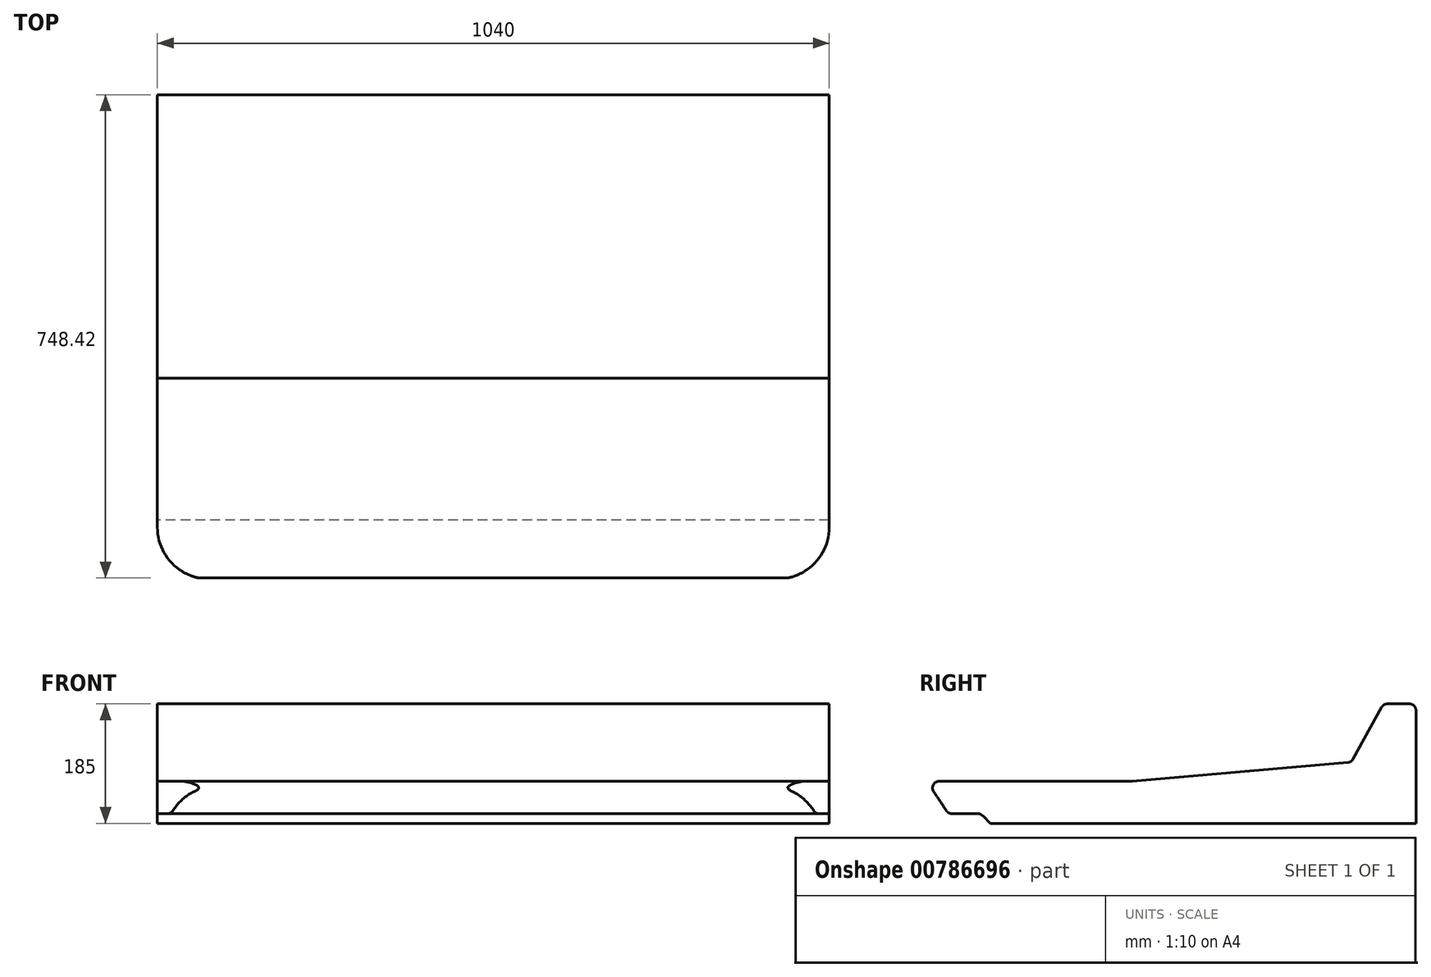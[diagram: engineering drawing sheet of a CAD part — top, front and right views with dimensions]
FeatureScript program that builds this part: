
annotation { "Feature Type Name" : "Feature", "Feature Type Description" : "" }
export const myFeature = defineFeature(function(context is Context, id is Id, definition is map)
    precondition{}
    {
        {
            var Q0;
            Q0=qCreatedBy(makeId("Right.planeOp"),FACE);
            var sketch = newSketch(context, id + "F0", { "sketchPlane" : qUnion([Q0])});
            skLineSegment(sketch, "E0", {"start": v(378, -92.5) * mm, "end": v(-281, -92.5) * mm});
            skLineSegment(sketch, "E1", {"start": v(-281, -92.5) * mm, "end": v(-293.07, -80.43) * mm});
            skLineSegment(sketch, "E2", {"start": v(-300.14, -77.5) * mm, "end": v(-340.62, -77.5) * mm});
            skLineSegment(sketch, "E3", {"start": v(-348.96, -73) * mm, "end": v(-368.76, -43) * mm});
            skLineSegment(sketch, "E4", {"start": v(-360.42, -27.5) * mm, "end": v(-61, -27.5) * mm});
            skLineSegment(sketch, "E5", {"start": v(-61, -27.5) * mm, "end": v(272.7, 1.7) * mm});
            skLineSegment(sketch, "E6", {"start": v(280.58, 6.81) * mm, "end": v(325.15, 87.34) * mm});
            skLineSegment(sketch, "E7", {"start": v(333.9, 92.5) * mm, "end": v(368, 92.5) * mm});
            skLineSegment(sketch, "E8", {"start": v(378, 82.5) * mm, "end": v(378, -92.5) * mm});
            skPoint(sketch, "E9.visualSharp", {"position": v(378, 92.5) * mm});
            skArc(sketch, "E9.filletArc", {"start": v(378, 82.5) * mm, "mid": v(375.07, 89.57) * mm, "end": v(368, 92.5) * mm});
            skPoint(sketch, "E10.visualSharp", {"position": v(328, 92.5) * mm});
            skArc(sketch, "E10.filletArc", {"start": v(333.9, 92.5) * mm, "mid": v(328.82, 91.11) * mm, "end": v(325.15, 87.34) * mm});
            skPoint(sketch, "E11.visualSharp", {"position": v(278, 2.16) * mm});
            skArc(sketch, "E11.filletArc", {"start": v(272.7, 1.7) * mm, "mid": v(277.28, 3.27) * mm, "end": v(280.58, 6.81) * mm});
            skPoint(sketch, "E12.visualSharp", {"position": v(-379, -27.5) * mm});
            skArc(sketch, "E12.filletArc", {"start": v(-360.42, -27.5) * mm, "mid": v(-369.22, -32.76) * mm, "end": v(-368.76, -43) * mm});
            skPoint(sketch, "E13.visualSharp", {"position": v(-346, -77.5) * mm});
            skArc(sketch, "E13.filletArc", {"start": v(-348.96, -73) * mm, "mid": v(-345.36, -76.3) * mm, "end": v(-340.62, -77.5) * mm});
            skPoint(sketch, "E14.visualSharp", {"position": v(-296, -77.5) * mm});
            skArc(sketch, "E14.filletArc", {"start": v(-293.07, -80.43) * mm, "mid": v(-296.32, -78.26) * mm, "end": v(-300.14, -77.5) * mm});
            skSolve(sketch);
        }
        {
            var Q0;
            Q0 = qSketchRegion(id + "F0", true);
            extrude(context, id + "F1", {"entities" : qUnion([Q0]), "endBound" : BoundingType.SYMMETRIC, "depth" : 1040 * mm, "offsetDistance" : 25 * mm});
        }
        {
            var Q0;
            Q0=makeQuery(id+"F1.opExtrude","SWEPT_FACE",FACE,{"disambiguationData":[OSD([sQuery(id+"F0.wireOp",EDGE,"E4")])]});
            var sketch = newSketch(context, id + "F2", { "sketchPlane" : qUnion([Q0])});
            skLineSegment(sketch, "E15", {"start": v(520, -272) * mm, "end": v(520, -292) * mm});
            skLineSegment(sketch, "E16", {"start": v(440, -372) * mm, "end": v(420, -372) * mm});
            skPoint(sketch, "E17.visualSharp", {"position": v(520, -372) * mm});
            skArc(sketch, "E17.filletArc", {"start": v(440, -372) * mm, "mid": v(496.57, -348.57) * mm, "end": v(520, -292) * mm});
            skLineSegment(sketch, "E18", {"start": v(420, -372) * mm, "end": v(415.92, -433.8) * mm});
            skLineSegment(sketch, "E19", {"start": v(415.92, -433.8) * mm, "end": v(574.9, -433.8) * mm});
            skLineSegment(sketch, "E20", {"start": v(574.9, -433.8) * mm, "end": v(520, -292) * mm});
            skLineSegment(sketch, "E21.MirrorCS", {"start": v(-415.92, -433.8) * mm, "end": v(-574.9, -433.8) * mm});
            skLineSegment(sketch, "E22.MirrorCS", {"start": v(-420, -372) * mm, "end": v(-415.92, -433.8) * mm});
            skArc(sketch, "E23.MirrorCS", {"start": v(-440, -372) * mm, "mid": v(-496.57, -348.57) * mm, "end": v(-520, -292) * mm});
            skLineSegment(sketch, "E24.MirrorCS", {"start": v(-440, -372) * mm, "end": v(-420, -372) * mm});
            skLineSegment(sketch, "E25.MirrorCS", {"start": v(-574.9, -433.8) * mm, "end": v(-520, -292) * mm});
            skSolve(sketch);
        }
        {
            var Q0;
            Q0 = qSketchRegion(id + "F2", true);
            extrude(context, id + "F3", {"entities" : qUnion([Q0]), "operationType" : NewBodyOperationType.REMOVE, "endBound" : BoundingType.THROUGH_ALL, "oppositeDirection" : true, "depth" : 25 * mm, "offsetDistance" : 25 * mm});
        }
    });
